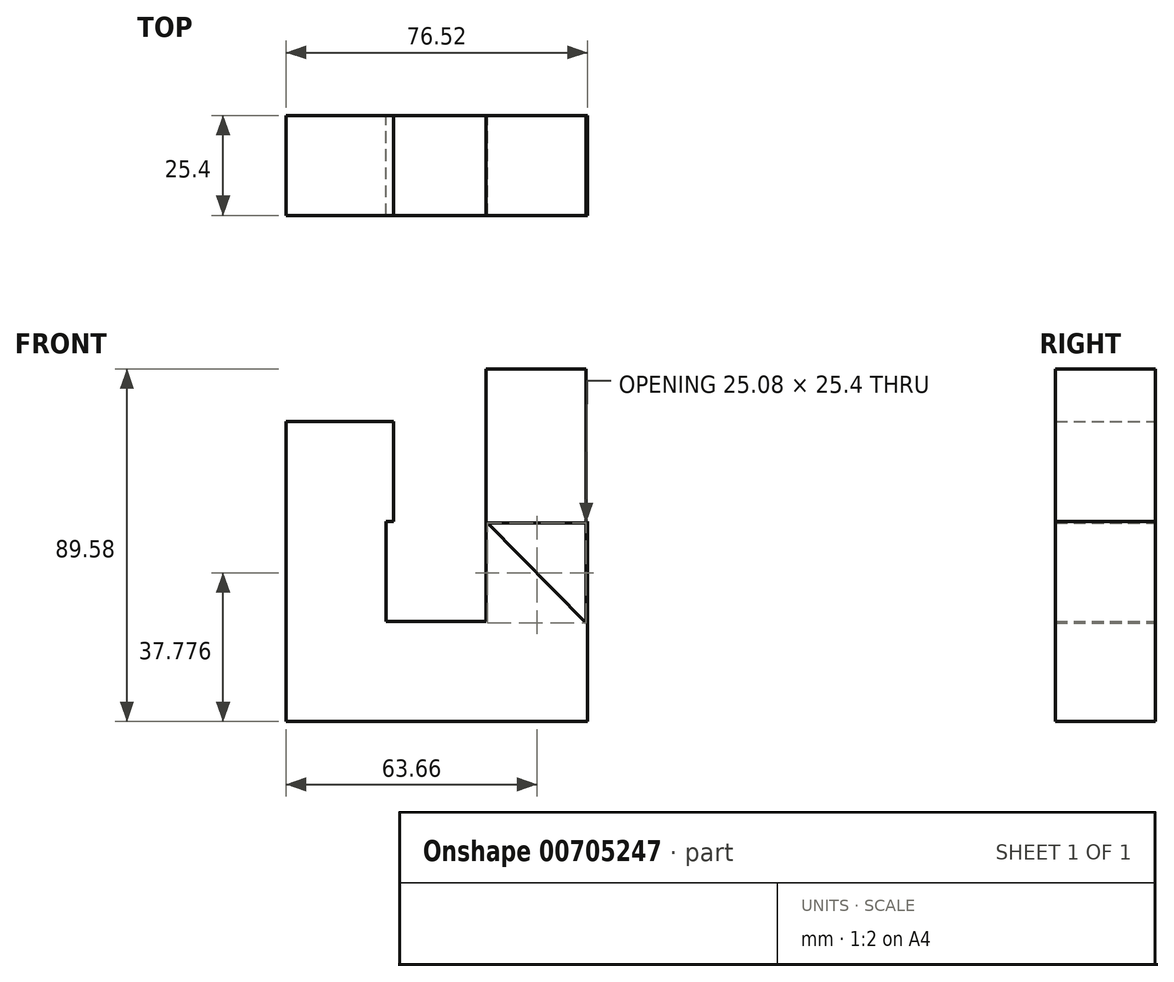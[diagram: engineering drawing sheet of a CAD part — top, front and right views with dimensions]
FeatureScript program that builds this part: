
annotation { "Feature Type Name" : "Feature", "Feature Type Description" : "" }
export const myFeature = defineFeature(function(context is Context, id is Id, definition is map)
    precondition{}
    {
        {
            var Q0;
            Q0=qCreatedBy(makeId("Front.planeOp"),FACE);
            var sketch = newSketch(context, id + "F0", { "sketchPlane" : qUnion([Q0])});
            skLineSegment(sketch, "E0.bottom", {"start": v(0, 0) * mm, "end": v(-25.4, 0) * mm});
            skLineSegment(sketch, "E0.top", {"start": v(0, 25.4) * mm, "end": v(-25.4, 25.4) * mm});
            skLineSegment(sketch, "E0.left", {"start": v(0, 0) * mm, "end": v(0, 25.4) * mm});
            skLineSegment(sketch, "E0.right", {"start": v(-25.4, 0) * mm, "end": v(-25.4, 25.4) * mm});
            skLineSegment(sketch, "E1.bottom", {"start": v(-25.4, 25.4) * mm, "end": v(-50.8, 25.4) * mm});
            skLineSegment(sketch, "E1.top", {"start": v(-25.4, 0) * mm, "end": v(-50.8, 0) * mm});
            skLineSegment(sketch, "E1.left", {"start": v(-25.4, 25.4) * mm, "end": v(-25.4, 0) * mm});
            skLineSegment(sketch, "E1.right", {"start": v(-50.8, 25.4) * mm, "end": v(-50.8, 0) * mm});
            skLineSegment(sketch, "E2.bottom", {"start": v(0, 25.4) * mm, "end": v(25.72, 25.4) * mm});
            skLineSegment(sketch, "E2.top", {"start": v(0, 0) * mm, "end": v(25.72, 0) * mm});
            skLineSegment(sketch, "E2.left", {"start": v(0, 25.4) * mm, "end": v(0, 0) * mm});
            skLineSegment(sketch, "E2.right", {"start": v(25.72, 25.4) * mm, "end": v(25.72, 0) * mm});
            skLineSegment(sketch, "E3.bottom", {"start": v(-50.8, 25.4) * mm, "end": v(-25.4, 25.4) * mm});
            skLineSegment(sketch, "E3.top", {"start": v(-50.8, 50.8) * mm, "end": v(-25.4, 50.8) * mm});
            skLineSegment(sketch, "E3.left", {"start": v(-50.8, 25.4) * mm, "end": v(-50.8, 50.8) * mm});
            skLineSegment(sketch, "E3.right", {"start": v(-25.4, 25.4) * mm, "end": v(-25.4, 50.8) * mm});
            skLineSegment(sketch, "E4.bottom", {"start": v(-50.8, 50.8) * mm, "end": v(-23.52, 50.8) * mm});
            skLineSegment(sketch, "E4.top", {"start": v(-50.8, 76.2) * mm, "end": v(-23.52, 76.2) * mm});
            skLineSegment(sketch, "E4.left", {"start": v(-50.8, 50.8) * mm, "end": v(-50.8, 76.2) * mm});
            skLineSegment(sketch, "E4.right", {"start": v(-23.52, 50.8) * mm, "end": v(-23.52, 76.2) * mm});
            skLineSegment(sketch, "E5.top", {"start": v(0, 50.8) * mm, "end": v(25.72, 50.8) * mm});
            skLineSegment(sketch, "E5.left", {"start": v(0, 25.4) * mm, "end": v(0, 50.8) * mm});
            skLineSegment(sketch, "E5.right", {"start": v(25.72, 25.4) * mm, "end": v(25.72, 50.8) * mm});
            skLineSegment(sketch, "E6.left", {"start": v(0, 50.8) * mm, "end": v(0, 75.88) * mm});
            skLineSegment(sketch, "E7.bottom", {"start": v(0, 50.8) * mm, "end": v(25.4, 25.08) * mm});
            skLineSegment(sketch, "E7.left", {"start": v(0, 50.8) * mm, "end": v(0, 64.18) * mm});
            skLineSegment(sketch, "E7.right", {"start": v(25.4, 25.08) * mm, "end": v(25.4, 50.48) * mm});
            skLineSegment(sketch, "E8.bottom", {"start": v(0, 75.88) * mm, "end": v(25.4, 75.88) * mm});
            skLineSegment(sketch, "E8.top", {"start": v(0, 50.48) * mm, "end": v(25.4, 50.48) * mm});
            skLineSegment(sketch, "E8.left", {"start": v(0, 50.48) * mm, "end": v(0, 75.88) * mm});
            skLineSegment(sketch, "E8.right", {"start": v(25.4, 50.48) * mm, "end": v(25.4, 75.88) * mm});
            skLineSegment(sketch, "E9.bottom", {"start": v(0, 64.18) * mm, "end": v(25.4, 64.18) * mm});
            skLineSegment(sketch, "E9.top", {"start": v(0, 89.58) * mm, "end": v(25.4, 89.58) * mm});
            skLineSegment(sketch, "E9.left", {"start": v(0, 64.18) * mm, "end": v(0, 89.58) * mm});
            skLineSegment(sketch, "E9.right", {"start": v(25.4, 64.18) * mm, "end": v(25.4, 89.58) * mm});
            skSolve(sketch);
        }
        {
            var Q0;
            Q0 = qSketchRegion(id + "F0", true);
            extrude(context, id + "F1", {"entities" : qUnion([Q0]), "depth" : 25.4 * mm, "offsetDistance" : 25.4 * mm});
        }
    });
